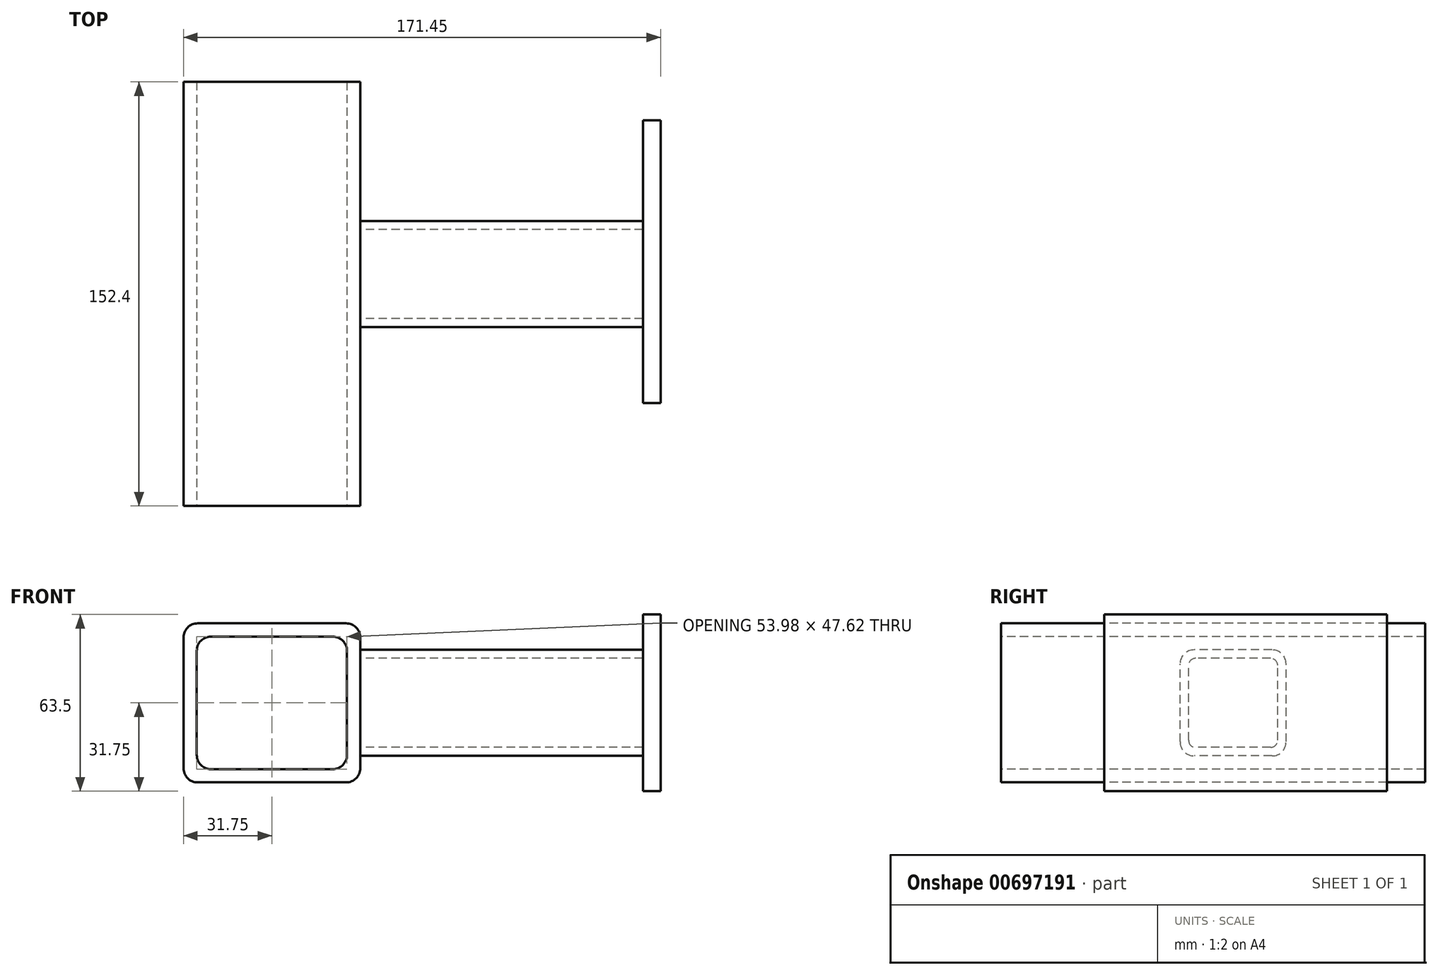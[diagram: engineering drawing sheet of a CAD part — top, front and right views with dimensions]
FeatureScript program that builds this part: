
annotation { "Feature Type Name" : "Feature", "Feature Type Description" : "" }
export const myFeature = defineFeature(function(context is Context, id is Id, definition is map)
    precondition{}
    {
        {
            var Q0;
            Q0=qCreatedBy(makeId("Front.planeOp"),FACE);
            var sketch = newSketch(context, id + "F0", { "sketchPlane" : qUnion([Q0])});
            skLineSegment(sketch, "E0.bottom", {"start": v(26.67, -28.57) * mm, "end": v(-26.67, -28.58) * mm});
            skLineSegment(sketch, "E0.top", {"start": v(26.67, 28.58) * mm, "end": v(-26.67, 28.57) * mm});
            skLineSegment(sketch, "E0.left", {"start": v(31.75, -23.5) * mm, "end": v(31.75, 23.5) * mm});
            skLineSegment(sketch, "E0.right", {"start": v(-31.75, -23.5) * mm, "end": v(-31.75, 23.5) * mm});
            skPoint(sketch, "E0.middle", {"position": v(0, 0) * mm});
            skLineSegment(sketch, "E1.0", {"start": v(21.9, 23.81) * mm, "end": v(-21.9, 23.81) * mm});
            skLineSegment(sketch, "E2.0", {"start": v(26.99, -18.73) * mm, "end": v(26.99, 18.73) * mm});
            skLineSegment(sketch, "E3.0", {"start": v(21.9, -23.81) * mm, "end": v(-21.9, -23.81) * mm});
            skLineSegment(sketch, "E4.0", {"start": v(-26.99, -18.73) * mm, "end": v(-26.99, 18.73) * mm});
            skPoint(sketch, "E5.visualSharp", {"position": v(-26.99, 23.81) * mm});
            skArc(sketch, "E5.filletArc", {"start": v(-21.9, 23.81) * mm, "mid": v(-25.5, 22.32) * mm, "end": v(-26.99, 18.73) * mm});
            skPoint(sketch, "E6.visualSharp", {"position": v(26.99, 23.81) * mm});
            skArc(sketch, "E6.filletArc", {"start": v(26.99, 18.73) * mm, "mid": v(25.5, 22.32) * mm, "end": v(21.9, 23.81) * mm});
            skPoint(sketch, "E7.visualSharp", {"position": v(26.99, -23.81) * mm});
            skArc(sketch, "E7.filletArc", {"start": v(21.9, -23.81) * mm, "mid": v(25.5, -22.32) * mm, "end": v(26.99, -18.73) * mm});
            skPoint(sketch, "E8.visualSharp", {"position": v(-26.99, -23.81) * mm});
            skArc(sketch, "E8.filletArc", {"start": v(-26.99, -18.73) * mm, "mid": v(-25.5, -22.32) * mm, "end": v(-21.9, -23.81) * mm});
            skPoint(sketch, "E9.visualSharp", {"position": v(-31.75, 28.57) * mm});
            skArc(sketch, "E9.filletArc", {"start": v(-26.67, 28.58) * mm, "mid": v(-30.26, 27.09) * mm, "end": v(-31.75, 23.5) * mm});
            skPoint(sketch, "E10.visualSharp", {"position": v(31.75, 28.58) * mm});
            skArc(sketch, "E10.filletArc", {"start": v(31.75, 23.5) * mm, "mid": v(30.26, 27.09) * mm, "end": v(26.67, 28.58) * mm});
            skPoint(sketch, "E11.visualSharp", {"position": v(-31.75, -28.58) * mm});
            skArc(sketch, "E11.filletArc", {"start": v(-31.75, -23.5) * mm, "mid": v(-30.26, -27.09) * mm, "end": v(-26.67, -28.58) * mm});
            skPoint(sketch, "E12.visualSharp", {"position": v(31.75, -28.57) * mm});
            skArc(sketch, "E12.filletArc", {"start": v(26.67, -28.57) * mm, "mid": v(30.26, -27.09) * mm, "end": v(31.75, -23.5) * mm});
            skSolve(sketch);
        }
        {
            var Q0;
            Q0=makeQuery(id+"F0.imprint","IMPRINT",FACE,{"disambiguationData":[TD([[makeQuery(id+"F0.imprint","IMPRINT",EDGE,{"derivedFrom":sQuery(id+"F0.wireOp",EDGE,"E0.bottom")}),-1.0]])]});
            extrude(context, id + "F1", {"entities" : qUnion([Q0]), "oppositeDirection" : true, "depth" : 152.4 * mm, "offsetDistance" : 25.4 * mm});
        }
        {
            var Q0;
            Q0=makeQuery(id+"F1.opExtrude","SWEPT_FACE",FACE,{"disambiguationData":[OSD([sQuery(id+"F0.wireOp",EDGE,"E0.left")])]});
            var sketch = newSketch(context, id + "F2", { "sketchPlane" : qUnion([Q0])});
            skLineSegment(sketch, "E13.bottom", {"start": v(97.37, -19.05) * mm, "end": v(69.43, -19.05) * mm});
            skLineSegment(sketch, "E13.top", {"start": v(97.37, 19.05) * mm, "end": v(69.43, 19.05) * mm});
            skLineSegment(sketch, "E13.left", {"start": v(102.45, -13.97) * mm, "end": v(102.45, 13.97) * mm});
            skLineSegment(sketch, "E13.right", {"start": v(64.35, -13.97) * mm, "end": v(64.35, 13.97) * mm});
            skPoint(sketch, "E13.middle", {"position": v(83.4, 0) * mm});
            skPoint(sketch, "E14.visualSharp", {"position": v(102.45, -19.05) * mm});
            skArc(sketch, "E14.filletArc", {"start": v(97.37, -19.05) * mm, "mid": v(100.96, -17.56) * mm, "end": v(102.45, -13.97) * mm});
            skPoint(sketch, "E15.visualSharp", {"position": v(102.45, 19.05) * mm});
            skArc(sketch, "E15.filletArc", {"start": v(102.45, 13.97) * mm, "mid": v(100.96, 17.56) * mm, "end": v(97.37, 19.05) * mm});
            skPoint(sketch, "E16.visualSharp", {"position": v(64.35, -19.05) * mm});
            skArc(sketch, "E16.filletArc", {"start": v(64.35, -13.97) * mm, "mid": v(65.83, -17.56) * mm, "end": v(69.43, -19.05) * mm});
            skPoint(sketch, "E17.visualSharp", {"position": v(64.35, 19.05) * mm});
            skArc(sketch, "E17.filletArc", {"start": v(69.43, 19.05) * mm, "mid": v(65.83, 17.56) * mm, "end": v(64.35, 13.97) * mm});
            skLineSegment(sketch, "E18.0", {"start": v(67.4, -13.46) * mm, "end": v(67.4, 13.46) * mm});
            skLineSegment(sketch, "E18.1", {"start": v(96.86, -16) * mm, "end": v(69.93, -16) * mm});
            skLineSegment(sketch, "E18.2", {"start": v(99.4, -13.46) * mm, "end": v(99.4, 13.46) * mm});
            skLineSegment(sketch, "E18.3", {"start": v(96.86, 16) * mm, "end": v(69.93, 16) * mm});
            skPoint(sketch, "E19.visualSharp", {"position": v(67.4, 16) * mm});
            skArc(sketch, "E19.filletArc", {"start": v(69.93, 16) * mm, "mid": v(68.14, 15.26) * mm, "end": v(67.4, 13.46) * mm});
            skPoint(sketch, "E20.visualSharp", {"position": v(99.4, 16) * mm});
            skArc(sketch, "E20.filletArc", {"start": v(99.4, 13.46) * mm, "mid": v(98.65, 15.26) * mm, "end": v(96.86, 16) * mm});
            skPoint(sketch, "E21.visualSharp", {"position": v(99.4, -16) * mm});
            skArc(sketch, "E21.filletArc", {"start": v(96.86, -16) * mm, "mid": v(98.65, -15.26) * mm, "end": v(99.4, -13.46) * mm});
            skPoint(sketch, "E22.visualSharp", {"position": v(67.4, -16) * mm});
            skArc(sketch, "E22.filletArc", {"start": v(67.4, -13.46) * mm, "mid": v(68.14, -15.26) * mm, "end": v(69.93, -16) * mm});
            skSolve(sketch);
        }
        {
            var Q0;
            Q0=makeQuery(id+"F2.imprint","IMPRINT",FACE,{"disambiguationData":[TD([[makeQuery(id+"F2.imprint","IMPRINT",EDGE,{"derivedFrom":sQuery(id+"F2.wireOp",EDGE,"E13.bottom")}),-1.0]])]});
            extrude(context, id + "F3", {"entities" : qUnion([Q0]), "operationType" : NewBodyOperationType.ADD, "depth" : 101.6 * mm, "offsetDistance" : 25.4 * mm});
        }
        {
            var Q0;
            Q0=makeQuery(id+"F3.opExtrude","CAP_FACE",FACE,{"disambiguationData":[OSD([sQuery(id+"F2.wireOp",EDGE,"E13.bottom"),sQuery(id+"F2.wireOp",EDGE,"E13.top"),sQuery(id+"F2.wireOp",EDGE,"E13.left"),sQuery(id+"F2.wireOp",EDGE,"E13.right"),sQuery(id+"F2.wireOp",EDGE,"E14.filletArc"),sQuery(id+"F2.wireOp",EDGE,"E15.filletArc"),sQuery(id+"F2.wireOp",EDGE,"E16.filletArc"),sQuery(id+"F2.wireOp",EDGE,"E17.filletArc"),sQuery(id+"F2.wireOp",EDGE,"E18.0"),sQuery(id+"F2.wireOp",EDGE,"E18.1"),sQuery(id+"F2.wireOp",EDGE,"E18.2"),sQuery(id+"F2.wireOp",EDGE,"E18.3"),sQuery(id+"F2.wireOp",EDGE,"E19.filletArc"),sQuery(id+"F2.wireOp",EDGE,"E20.filletArc"),sQuery(id+"F2.wireOp",EDGE,"E21.filletArc"),sQuery(id+"F2.wireOp",EDGE,"E22.filletArc")])],"isStart":false});
            var sketch = newSketch(context, id + "F4", { "sketchPlane" : qUnion([Q0])});
            skLineSegment(sketch, "E23.bottom", {"start": v(138.63, -31.75) * mm, "end": v(37.03, -31.75) * mm});
            skLineSegment(sketch, "E23.top", {"start": v(138.63, 31.75) * mm, "end": v(37.03, 31.75) * mm});
            skLineSegment(sketch, "E23.left", {"start": v(138.63, -31.75) * mm, "end": v(138.63, 31.75) * mm});
            skLineSegment(sketch, "E23.right", {"start": v(37.03, -31.75) * mm, "end": v(37.03, 31.75) * mm});
            skPoint(sketch, "E23.middle", {"position": v(87.83, 0) * mm});
            skSolve(sketch);
        }
        {
            var Q0;
            Q0=makeQuery(id+"F4.imprint","IMPRINT",FACE,{"disambiguationData":[TD([[makeQuery(id+"F4.imprint","IMPRINT",EDGE,{"derivedFrom":sQuery(id+"F4.wireOp",EDGE,"E23.bottom")}),-1.0]])]});
            var sketch = newSketch(context, id + "F5", { "sketchPlane" : qUnion([Q0])});
            skSolve(sketch);
        }
        {
            var Q0;
            Q0=makeQuery(id+"F4.imprint","IMPRINT",FACE,{"disambiguationData":[TD([[makeQuery(id+"F4.imprint","IMPRINT",EDGE,{"derivedFrom":makeQuery(id+"F3.opExtrude","CAP_EDGE",EDGE,{"disambiguationData":[OSD([sQuery(id+"F2.wireOp",EDGE,"E18.0")])],"isStart":false})}),-1.0]])]});
            var Q1;
            Q1=makeQuery(id+"F4.imprint","IMPRINT",FACE,{"disambiguationData":[TD([[makeQuery(id+"F4.imprint","IMPRINT",EDGE,{"derivedFrom":makeQuery(id+"F3.opExtrude","CAP_EDGE",EDGE,{"disambiguationData":[OSD([sQuery(id+"F2.wireOp",EDGE,"E13.bottom")])],"isStart":false})}),-1.0]])]});
            var Q2;
            Q2=makeQuery(id+"F5.imprint","IMPRINT",FACE,{"disambiguationData":[TD([[makeQuery(id+"F5.imprint","IMPRINT",EDGE,{"derivedFrom":makeQuery(id+"F4.imprint","IMPRINT",EDGE,{"derivedFrom":sQuery(id+"F4.wireOp",EDGE,"E23.bottom")})}),-1.0]])]});
            extrude(context, id + "F6", {"entities" : qUnion([Q0, Q1, Q2]), "operationType" : NewBodyOperationType.ADD, "depth" : 6.35 * mm, "offsetDistance" : 25.4 * mm});
        }
    });
